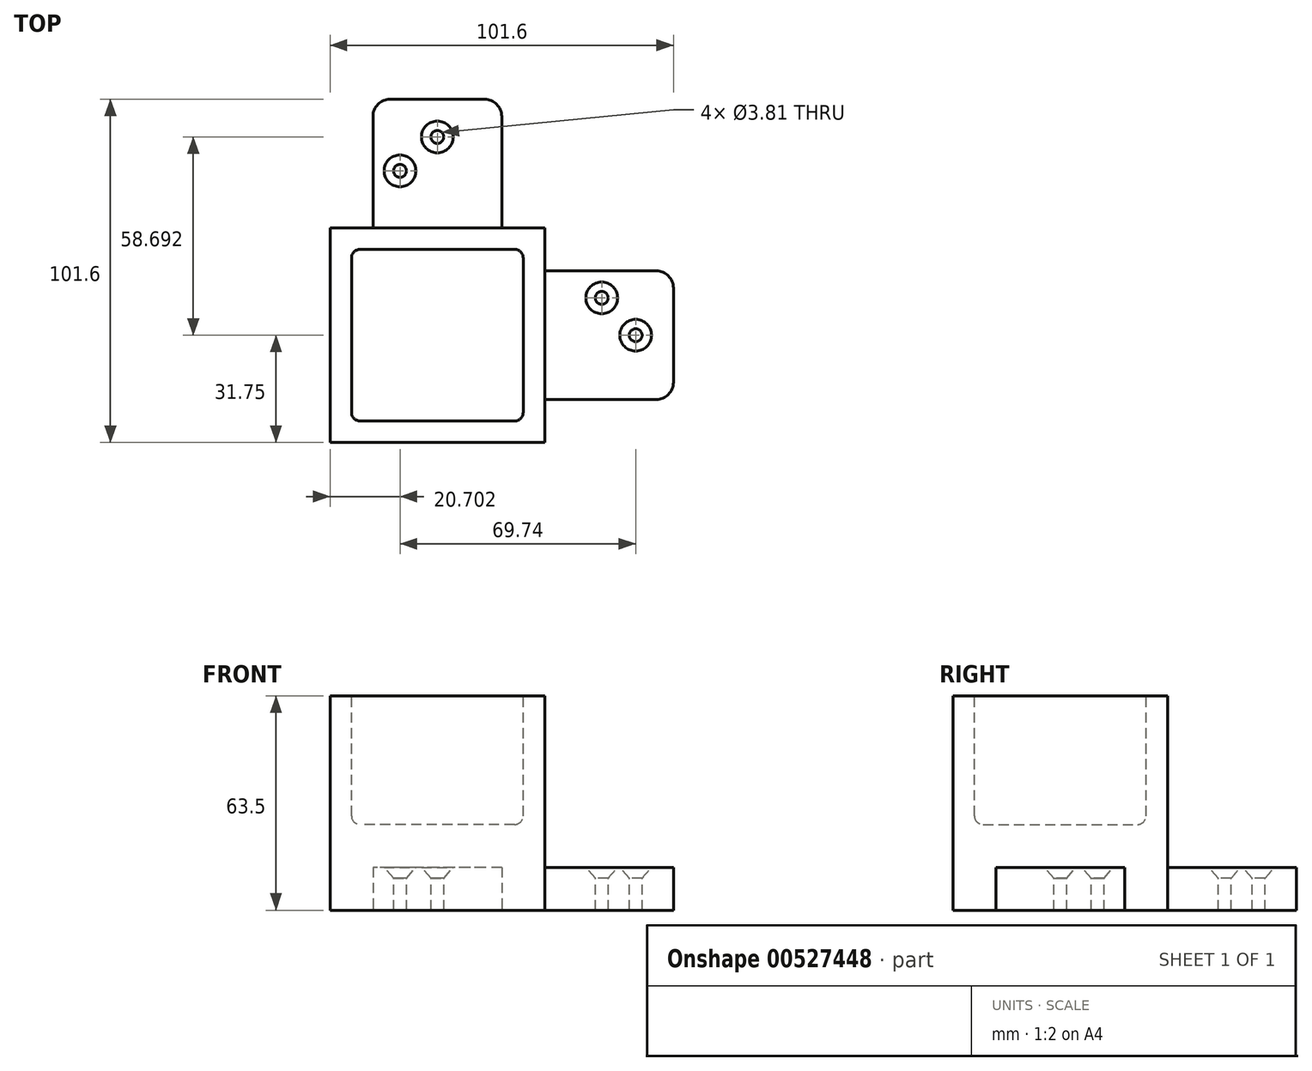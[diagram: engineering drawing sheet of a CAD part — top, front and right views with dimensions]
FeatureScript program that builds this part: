
annotation { "Feature Type Name" : "Feature", "Feature Type Description" : "" }
export const myFeature = defineFeature(function(context is Context, id is Id, definition is map)
    precondition{}
    {
        {
            var Q0;
            Q0=qCreatedBy(makeId("Top.planeOp"),FACE);
            var sketch = newSketch(context, id + "F0", { "sketchPlane" : qUnion([Q0])});
            skLineSegment(sketch, "E0.bottom", {"start": v(31.75, -31.75) * mm, "end": v(-31.75, -31.75) * mm});
            skLineSegment(sketch, "E0.top", {"start": v(31.75, 31.75) * mm, "end": v(-31.75, 31.75) * mm});
            skLineSegment(sketch, "E0.left", {"start": v(31.75, -31.75) * mm, "end": v(31.75, 31.75) * mm});
            skLineSegment(sketch, "E0.right", {"start": v(-31.75, -31.75) * mm, "end": v(-31.75, 31.75) * mm});
            skPoint(sketch, "E0.middle", {"position": v(0, 0) * mm});
            skSolve(sketch);
        }
        {
            var Q0;
            Q0=makeQuery(id+"F0.imprint","IMPRINT",FACE,{"disambiguationData":[TD([[makeQuery(id+"F0.imprint","IMPRINT",EDGE,{"derivedFrom":sQuery(id+"F0.wireOp",EDGE,"E0.bottom")}),-1.0]])]});
            extrude(context, id + "F1", {"entities" : qUnion([Q0]), "depth" : 63.5 * mm, "offsetDistance" : 25.4 * mm});
        }
        {
            var Q0;
            Q0=makeQuery(id+"F1.opExtrude","CAP_FACE",FACE,{"disambiguationData":[OSD([sQuery(id+"F0.wireOp",EDGE,"E0.bottom"),sQuery(id+"F0.wireOp",EDGE,"E0.top"),sQuery(id+"F0.wireOp",EDGE,"E0.left"),sQuery(id+"F0.wireOp",EDGE,"E0.right")])],"isStart":false});
            var sketch = newSketch(context, id + "F2", { "sketchPlane" : qUnion([Q0])});
            skLineSegment(sketch, "E1.0", {"start": v(25.4, -25.4) * mm, "end": v(25.4, 25.4) * mm});
            skLineSegment(sketch, "E1.1", {"start": v(-25.4, -25.4) * mm, "end": v(25.4, -25.4) * mm});
            skLineSegment(sketch, "E1.2", {"start": v(-25.4, 25.4) * mm, "end": v(-25.4, -25.4) * mm});
            skLineSegment(sketch, "E1.3", {"start": v(25.4, 25.4) * mm, "end": v(-25.4, 25.4) * mm});
            skSolve(sketch);
        }
        {
            var Q0;
            Q0 = qSketchRegion(id + "F2", true);
            extrude(context, id + "F3", {"entities" : qUnion([Q0]), "operationType" : NewBodyOperationType.REMOVE, "oppositeDirection" : true, "depth" : 38.1 * mm, "offsetDistance" : 25.4 * mm});
        }
        {
            var Q0;
            Q0=qCreatedBy(makeId("Top.planeOp"),FACE);
            var sketch = newSketch(context, id + "F4", { "sketchPlane" : qUnion([Q0])});
            skLineSegment(sketch, "E2.bottom", {"start": v(69.85, -19.05) * mm, "end": v(31.75, -19.05) * mm});
            skLineSegment(sketch, "E2.top", {"start": v(69.85, 19.05) * mm, "end": v(31.75, 19.05) * mm});
            skLineSegment(sketch, "E2.left", {"start": v(69.85, -19.05) * mm, "end": v(69.85, 19.05) * mm});
            skLineSegment(sketch, "E2.right", {"start": v(31.75, -19.05) * mm, "end": v(31.75, 19.05) * mm});
            skPoint(sketch, "E2.middle", {"position": v(50.8, 0) * mm});
            skLineSegment(sketch, "E3.0", {"start": v(31.75, -31.75) * mm, "end": v(31.75, 31.75) * mm});
            skSolve(sketch);
        }
        {
            var Q0;
            {var subQ0=sQuery(id+"F4.wireOp",EDGE,"E2.bottom");Q0=makeQuery(id+"F4.imprint","IMPRINT",FACE,{"disambiguationData":[TD([[makeQuery(id+"F4.imprint","IMPRINT",EDGE,{"derivedFrom":subQ0}),-1.0]])]});}
            extrude(context, id + "F5", {"entities" : qUnion([Q0]), "depth" : 12.7 * mm, "offsetDistance" : 25.4 * mm});
        }
        {
            var Q0;
            Q0=makeQuery(id+"F5.opExtrude","SWEPT_EDGE",EDGE,{"disambiguationData":[OSD([sQuery(id+"F4.wireOp",EDGE,"E2.bottom"),sQuery(id+"F4.wireOp",EDGE,"E2.left")])]});
            var Q1;
            Q1=makeQuery(id+"F5.opExtrude","SWEPT_EDGE",EDGE,{"disambiguationData":[OSD([sQuery(id+"F4.wireOp",EDGE,"E2.top"),sQuery(id+"F4.wireOp",EDGE,"E2.left")])]});
            fillet(context, id + "F6", {"entities" : qUnion([Q0, Q1]), "radius" : 5.08 * mm, "tangentPropagation" : true, "allowEdgeOverflow" : false});
        }
        {
            var Q0;
            Q0=makeQuery(id+"F5.opExtrude","CAP_FACE",FACE,{"disambiguationData":[OSD([sQuery(id+"F4.wireOp",EDGE,"E2.bottom"),sQuery(id+"F4.wireOp",EDGE,"E2.top"),sQuery(id+"F4.wireOp",EDGE,"E2.left"),sQuery(id+"F4.wireOp",EDGE,"E3.0")])],"isStart":false});
            var sketch = newSketch(context, id + "F7", { "sketchPlane" : qUnion([Q0])});
            skLineSegment(sketch, "E4", {"start": v(58.7, 0) * mm, "end": v(58.7, 11.05) * mm});
            skLineSegment(sketch, "E5", {"start": v(58.7, 11.05) * mm, "end": v(48.64, 11.05) * mm});
            skLineSegment(sketch, "E6", {"start": v(48.64, 11.05) * mm, "end": v(58.7, 0) * mm});
            skSolve(sketch);
        }
        {
            var Q0;
            Q0=sQuery(id+"F7.wireOp",VERTEX,"E4.start");
            var Q1;
            Q1=sQuery(id+"F7.wireOp",VERTEX,"E6.start");
            var Q2;
            Q2=makeQuery(id+"F5.opExtrude","SWEPT_BODY",BODY,{"disambiguationData":[OSD([sQuery(id+"F4.wireOp",EDGE,"E2.bottom"),sQuery(id+"F4.wireOp",EDGE,"E2.top"),sQuery(id+"F4.wireOp",EDGE,"E2.left"),sQuery(id+"F4.wireOp",EDGE,"E3.0")])]});
            hole(context, id + "F8", {"style" : HoleStyle.C_SINK, "endStyle" : HoleEndStyle.THROUGH, "holeDiameter" : 3.8 * mm, "cSinkDiameter" : 9.4 * mm, "cSinkAngle" : 82 * degree, "isTappedThrough" : true, "tappedDepth" : 12.7 * mm, "tapClearance" : 3, "locations" : qUnion([Q0, Q1]), "scope" : qUnion([Q2])});
        }
        {
            var Q0;
            Q0=qCreatedBy(makeId("Right.planeOp"),FACE);
            var sketch = newSketch(context, id + "F9", { "sketchPlane" : qUnion([Q0])});
            skLineSegment(sketch, "E7", {"start": v(0, 73.59) * mm, "end": v(0, 0) * mm});
            skSolve(sketch);
        }
        {
            var Q0;
            Q0=makeQuery(id+"F5.opExtrude","SWEPT_BODY",BODY,{"disambiguationData":[OSD([sQuery(id+"F4.wireOp",EDGE,"E2.bottom"),sQuery(id+"F4.wireOp",EDGE,"E2.top"),sQuery(id+"F4.wireOp",EDGE,"E2.left"),sQuery(id+"F4.wireOp",EDGE,"E3.0")])]});
            var Q1;
            Q1=sQuery(id+"F9.wireOp",EDGE,"E7");
            circularPattern(context, id + "F10", {"entities" : qUnion([Q0]), "axis" : qUnion([Q1]), "angle" : 90 * degree, "instanceCount" : 2, "oppositeDirection" : true, "equalSpace" : true});
        }
        {
            var Q0;
            Q0=makeQuery(id+"F3.boolean.opBoolean","COPY",FACE,{"derivedFrom":makeQuery(id+"F3.opExtrude","CAP_FACE",FACE,{"disambiguationData":[OSD([sQuery(id+"F2.wireOp",EDGE,"E1.0"),sQuery(id+"F2.wireOp",EDGE,"E1.1"),sQuery(id+"F2.wireOp",EDGE,"E1.2"),sQuery(id+"F2.wireOp",EDGE,"E1.3")])],"isStart":false})});
            var Q1;
            Q1=makeQuery(id+"F3.boolean.opBoolean","COPY",EDGE,{"derivedFrom":makeQuery(id+"F3.opExtrude","SWEPT_EDGE",EDGE,{"disambiguationData":[OSD([sQuery(id+"F2.wireOp",EDGE,"E1.2"),sQuery(id+"F2.wireOp",EDGE,"E1.3")])]})});
            var Q2;
            Q2=makeQuery(id+"F3.boolean.opBoolean","COPY",EDGE,{"derivedFrom":makeQuery(id+"F3.opExtrude","SWEPT_EDGE",EDGE,{"disambiguationData":[OSD([sQuery(id+"F2.wireOp",EDGE,"E1.0"),sQuery(id+"F2.wireOp",EDGE,"E1.3")])]})});
            var Q3;
            Q3=makeQuery(id+"F3.boolean.opBoolean","COPY",EDGE,{"derivedFrom":makeQuery(id+"F3.opExtrude","SWEPT_EDGE",EDGE,{"disambiguationData":[OSD([sQuery(id+"F2.wireOp",EDGE,"E1.0"),sQuery(id+"F2.wireOp",EDGE,"E1.1")])]})});
            var Q4;
            Q4=makeQuery(id+"F3.boolean.opBoolean","COPY",EDGE,{"derivedFrom":makeQuery(id+"F3.opExtrude","SWEPT_EDGE",EDGE,{"disambiguationData":[OSD([sQuery(id+"F2.wireOp",EDGE,"E1.1"),sQuery(id+"F2.wireOp",EDGE,"E1.2")])]})});
            fillet(context, id + "F11", {"entities" : qUnion([Q0, Q1, Q2, Q3, Q4]), "radius" : 2.54 * mm, "tangentPropagation" : true, "allowEdgeOverflow" : false});
        }
    });
